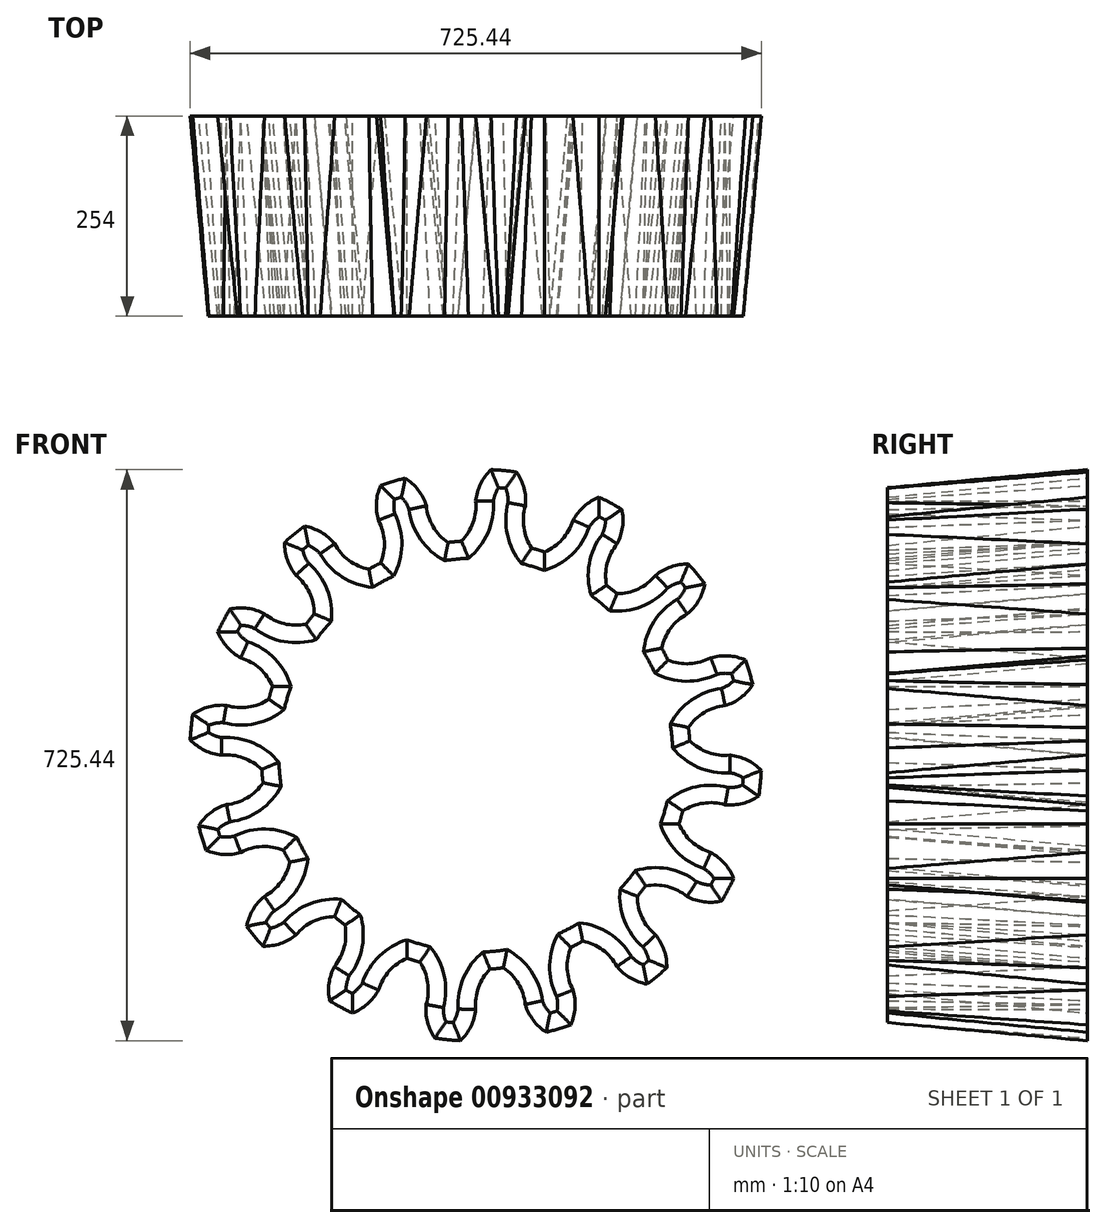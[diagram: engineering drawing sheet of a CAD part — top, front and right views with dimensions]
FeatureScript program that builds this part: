
annotation { "Feature Type Name" : "Feature", "Feature Type Description" : "" }
export const myFeature = defineFeature(function(context is Context, id is Id, definition is map)
    precondition{}
    {
        {
            var Q0;
            Q0=qCreatedBy(makeId("Front.planeOp"),FACE);
            var sketch = newSketch(context, id + "F0", { "sketchPlane" : qUnion([Q0])});
            skArc(sketch, "E0", {"start": v(19.52, 362.72) * mm, "mid": v(6.16, 344.56) * mm, "end": v(0, 322.88) * mm});
            skArc(sketch, "E1", {"start": v(63.13, 316.65) * mm, "mid": v(61.06, 288.95) * mm, "end": v(71.04, 263.02) * mm});
            skArc(sketch, "E2", {"start": v(51.78, 359.54) * mm, "mid": v(35.68, 361.49) * mm, "end": v(19.52, 362.72) * mm});
            skCircle(sketch, "E3", {"center": v(0, 0) * mm, "radius": 272.44 * mm});
            skArc(sketch, "E4.trimOffspring", {"start": v(-18.24, 271.83) * mm, "mid": v(-3.4, 295.31) * mm, "end": v(0, 322.88) * mm});
            skArc(sketch, "E5.trimOffspring", {"start": v(63.13, 316.65) * mm, "mid": v(61.32, 339.12) * mm, "end": v(51.78, 359.54) * mm});
            skArc(sketch, "E6.1.0", {"start": v(-89.75, 351.98) * mm, "mid": v(-105.37, 347.63) * mm, "end": v(-120.77, 342.58) * mm});
            skArc(sketch, "E6.1.1", {"start": v(-62.85, 316.7) * mm, "mid": v(-73.12, 336.77) * mm, "end": v(-89.75, 351.98) * mm});
            skArc(sketch, "E6.1.2", {"start": v(-62.85, 316.7) * mm, "mid": v(-54.16, 290.32) * mm, "end": v(-35.02, 270.18) * mm});
            skArc(sketch, "E6.1.4", {"start": v(-120.88, 244.16) * mm, "mid": v(-116.14, 271.53) * mm, "end": v(-123.56, 298.3) * mm});
            skArc(sketch, "E6.1.5", {"start": v(-120.77, 342.58) * mm, "mid": v(-126.16, 320.7) * mm, "end": v(-123.56, 298.3) * mm});
            skArc(sketch, "E6.2.0", {"start": v(-217.62, 290.84) * mm, "mid": v(-230.38, 280.84) * mm, "end": v(-242.68, 270.28) * mm});
            skArc(sketch, "E6.2.1", {"start": v(-179.27, 268.55) * mm, "mid": v(-196.43, 283.16) * mm, "end": v(-217.62, 290.84) * mm});
            skArc(sketch, "E6.2.2", {"start": v(-179.27, 268.55) * mm, "mid": v(-161.14, 247.5) * mm, "end": v(-135.75, 236.21) * mm});
            skArc(sketch, "E6.2.4", {"start": v(-205.11, 179.31) * mm, "mid": v(-211.21, 206.42) * mm, "end": v(-228.31, 228.31) * mm});
            skArc(sketch, "E6.2.5", {"start": v(-242.68, 270.28) * mm, "mid": v(-239.29, 248) * mm, "end": v(-228.31, 228.31) * mm});
            skArc(sketch, "E7.1.3.0", {"start": v(-312.35, 185.42) * mm, "mid": v(-320.32, 171.3) * mm, "end": v(-327.64, 156.84) * mm});
            skArc(sketch, "E7.4.3.0", {"start": v(-268.4, 179.5) * mm, "mid": v(-289.84, 186.43) * mm, "end": v(-312.35, 185.42) * mm});
            skArc(sketch, "E7.8.3.0", {"start": v(-268.4, 179.5) * mm, "mid": v(-243.58, 167) * mm, "end": v(-215.81, 166.28) * mm});
            skArc(sketch, "E7.12.3.0", {"start": v(271.83, 18.24) * mm, "mid": v(-271.12, 26.76) * mm, "end": v(263.02, -71.04) * mm});
            skArc(sketch, "E7.14.3.0", {"start": v(-258.12, 87.17) * mm, "mid": v(-274.13, 109.88) * mm, "end": v(-298.3, 123.56) * mm});
            skArc(sketch, "E7.18.3.0", {"start": v(-327.64, 156.84) * mm, "mid": v(-315.98, 137.55) * mm, "end": v(-298.3, 123.56) * mm});
            skArc(sketch, "E7.1.4.0", {"start": v(-359.54, 51.78) * mm, "mid": v(-361.49, 35.68) * mm, "end": v(-362.72, 19.52) * mm});
            skArc(sketch, "E7.4.4.0", {"start": v(-316.65, 63.13) * mm, "mid": v(-339.12, 61.32) * mm, "end": v(-359.54, 51.78) * mm});
            skArc(sketch, "E7.8.4.0", {"start": v(-316.65, 63.13) * mm, "mid": v(-288.95, 61.06) * mm, "end": v(-263.02, 71.04) * mm});
            skArc(sketch, "E7.14.4.0", {"start": v(-271.83, -18.24) * mm, "mid": v(-295.31, -3.4) * mm, "end": v(-322.88, 0) * mm});
            skArc(sketch, "E7.18.4.0", {"start": v(-362.72, 19.52) * mm, "mid": v(-344.56, 6.16) * mm, "end": v(-322.88, 0) * mm});
            skArc(sketch, "E7.1.5.0", {"start": v(-351.98, -89.75) * mm, "mid": v(-347.63, -105.37) * mm, "end": v(-342.58, -120.77) * mm});
            skArc(sketch, "E7.4.5.0", {"start": v(-316.7, -62.85) * mm, "mid": v(-336.77, -73.12) * mm, "end": v(-351.98, -89.75) * mm});
            skArc(sketch, "E7.8.5.0", {"start": v(-316.7, -62.85) * mm, "mid": v(-290.32, -54.16) * mm, "end": v(-270.18, -35.02) * mm});
            skArc(sketch, "E7.14.5.0", {"start": v(-244.16, -120.88) * mm, "mid": v(-271.53, -116.14) * mm, "end": v(-298.3, -123.56) * mm});
            skArc(sketch, "E7.18.5.0", {"start": v(-342.58, -120.77) * mm, "mid": v(-320.7, -126.16) * mm, "end": v(-298.3, -123.56) * mm});
            skArc(sketch, "E7.1.6.0", {"start": v(-290.84, -217.62) * mm, "mid": v(-280.84, -230.38) * mm, "end": v(-270.28, -242.68) * mm});
            skArc(sketch, "E7.4.6.0", {"start": v(-268.55, -179.27) * mm, "mid": v(-283.16, -196.43) * mm, "end": v(-290.84, -217.62) * mm});
            skArc(sketch, "E7.8.6.0", {"start": v(-268.55, -179.27) * mm, "mid": v(-247.5, -161.14) * mm, "end": v(-236.21, -135.75) * mm});
            skArc(sketch, "E7.14.6.0", {"start": v(-179.31, -205.11) * mm, "mid": v(-206.42, -211.21) * mm, "end": v(-228.31, -228.31) * mm});
            skArc(sketch, "E7.18.6.0", {"start": v(-270.28, -242.68) * mm, "mid": v(-248, -239.29) * mm, "end": v(-228.31, -228.31) * mm});
            skArc(sketch, "E7.1.7.0", {"start": v(-185.42, -312.35) * mm, "mid": v(-171.3, -320.32) * mm, "end": v(-156.84, -327.64) * mm});
            skArc(sketch, "E7.4.7.0", {"start": v(-179.5, -268.4) * mm, "mid": v(-186.43, -289.84) * mm, "end": v(-185.42, -312.35) * mm});
            skArc(sketch, "E7.8.7.0", {"start": v(-179.5, -268.4) * mm, "mid": v(-167, -243.58) * mm, "end": v(-166.28, -215.81) * mm});
            skArc(sketch, "E7.14.7.0", {"start": v(-87.17, -258.12) * mm, "mid": v(-109.88, -274.13) * mm, "end": v(-123.56, -298.3) * mm});
            skArc(sketch, "E7.18.7.0", {"start": v(-156.84, -327.64) * mm, "mid": v(-137.55, -315.98) * mm, "end": v(-123.56, -298.3) * mm});
            skArc(sketch, "E7.1.8.0", {"start": v(-51.78, -359.54) * mm, "mid": v(-35.68, -361.49) * mm, "end": v(-19.52, -362.72) * mm});
            skArc(sketch, "E7.4.8.0", {"start": v(-63.13, -316.65) * mm, "mid": v(-61.32, -339.12) * mm, "end": v(-51.78, -359.54) * mm});
            skArc(sketch, "E7.8.8.0", {"start": v(-63.13, -316.65) * mm, "mid": v(-61.06, -288.95) * mm, "end": v(-71.04, -263.02) * mm});
            skArc(sketch, "E7.12.8.0", {"start": v(271.83, 18.24) * mm, "mid": v(-260.7, 79.14) * mm, "end": v(215.81, -166.28) * mm});
            skArc(sketch, "E7.14.8.0", {"start": v(18.24, -271.83) * mm, "mid": v(3.4, -295.31) * mm, "end": v(0, -322.88) * mm});
            skArc(sketch, "E7.18.8.0", {"start": v(-19.52, -362.72) * mm, "mid": v(-6.16, -344.56) * mm, "end": v(0, -322.88) * mm});
            skArc(sketch, "E7.1.9.0", {"start": v(89.75, -351.98) * mm, "mid": v(105.37, -347.63) * mm, "end": v(120.77, -342.58) * mm});
            skArc(sketch, "E7.4.9.0", {"start": v(62.85, -316.7) * mm, "mid": v(73.12, -336.77) * mm, "end": v(89.75, -351.98) * mm});
            skArc(sketch, "E7.8.9.0", {"start": v(62.85, -316.7) * mm, "mid": v(54.16, -290.32) * mm, "end": v(35.02, -270.18) * mm});
            skArc(sketch, "E7.14.9.0", {"start": v(120.88, -244.16) * mm, "mid": v(116.14, -271.53) * mm, "end": v(123.56, -298.3) * mm});
            skArc(sketch, "E7.18.9.0", {"start": v(120.77, -342.58) * mm, "mid": v(126.16, -320.7) * mm, "end": v(123.56, -298.3) * mm});
            skArc(sketch, "E7.1.10.0", {"start": v(217.62, -290.84) * mm, "mid": v(230.38, -280.84) * mm, "end": v(242.68, -270.28) * mm});
            skArc(sketch, "E7.4.10.0", {"start": v(179.27, -268.55) * mm, "mid": v(196.43, -283.16) * mm, "end": v(217.62, -290.84) * mm});
            skArc(sketch, "E7.8.10.0", {"start": v(179.27, -268.55) * mm, "mid": v(161.14, -247.5) * mm, "end": v(135.75, -236.21) * mm});
            skArc(sketch, "E7.14.10.0", {"start": v(205.11, -179.31) * mm, "mid": v(211.21, -206.42) * mm, "end": v(228.31, -228.31) * mm});
            skArc(sketch, "E7.18.10.0", {"start": v(242.68, -270.28) * mm, "mid": v(239.29, -248) * mm, "end": v(228.31, -228.31) * mm});
            skArc(sketch, "E7.1.11.0", {"start": v(312.35, -185.42) * mm, "mid": v(320.32, -171.3) * mm, "end": v(327.64, -156.84) * mm});
            skArc(sketch, "E7.4.11.0", {"start": v(268.4, -179.5) * mm, "mid": v(289.84, -186.43) * mm, "end": v(312.35, -185.42) * mm});
            skArc(sketch, "E7.8.11.0", {"start": v(268.4, -179.5) * mm, "mid": v(243.58, -167) * mm, "end": v(215.81, -166.28) * mm});
            skArc(sketch, "E7.14.11.0", {"start": v(258.12, -87.17) * mm, "mid": v(274.13, -109.88) * mm, "end": v(298.3, -123.56) * mm});
            skArc(sketch, "E7.18.11.0", {"start": v(327.64, -156.84) * mm, "mid": v(315.98, -137.55) * mm, "end": v(298.3, -123.56) * mm});
            skArc(sketch, "E7.1.12.0", {"start": v(359.54, -51.78) * mm, "mid": v(361.49, -35.68) * mm, "end": v(362.72, -19.52) * mm});
            skArc(sketch, "E7.4.12.0", {"start": v(316.65, -63.13) * mm, "mid": v(339.12, -61.32) * mm, "end": v(359.54, -51.78) * mm});
            skArc(sketch, "E7.8.12.0", {"start": v(316.65, -63.13) * mm, "mid": v(288.95, -61.06) * mm, "end": v(263.02, -71.04) * mm});
            skArc(sketch, "E7.14.12.0", {"start": v(271.83, 18.24) * mm, "mid": v(295.31, 3.4) * mm, "end": v(322.88, 0) * mm});
            skArc(sketch, "E7.18.12.0", {"start": v(362.72, -19.52) * mm, "mid": v(344.56, -6.16) * mm, "end": v(322.88, 0) * mm});
            skArc(sketch, "E7.1.13.0", {"start": v(351.98, 89.75) * mm, "mid": v(347.63, 105.37) * mm, "end": v(342.58, 120.77) * mm});
            skArc(sketch, "E7.4.13.0", {"start": v(316.7, 62.85) * mm, "mid": v(336.77, 73.12) * mm, "end": v(351.98, 89.75) * mm});
            skArc(sketch, "E7.8.13.0", {"start": v(316.7, 62.85) * mm, "mid": v(290.32, 54.16) * mm, "end": v(270.18, 35.02) * mm});
            skArc(sketch, "E7.14.13.0", {"start": v(244.16, 120.88) * mm, "mid": v(271.53, 116.14) * mm, "end": v(298.3, 123.56) * mm});
            skArc(sketch, "E7.18.13.0", {"start": v(342.58, 120.77) * mm, "mid": v(320.7, 126.16) * mm, "end": v(298.3, 123.56) * mm});
            skArc(sketch, "E7.1.14.0", {"start": v(290.84, 217.62) * mm, "mid": v(280.84, 230.38) * mm, "end": v(270.28, 242.68) * mm});
            skArc(sketch, "E7.4.14.0", {"start": v(268.55, 179.27) * mm, "mid": v(283.16, 196.43) * mm, "end": v(290.84, 217.62) * mm});
            skArc(sketch, "E7.8.14.0", {"start": v(268.55, 179.27) * mm, "mid": v(247.5, 161.14) * mm, "end": v(236.21, 135.75) * mm});
            skArc(sketch, "E7.14.14.0", {"start": v(179.31, 205.11) * mm, "mid": v(206.42, 211.21) * mm, "end": v(228.31, 228.31) * mm});
            skArc(sketch, "E7.18.14.0", {"start": v(270.28, 242.68) * mm, "mid": v(248, 239.29) * mm, "end": v(228.31, 228.31) * mm});
            skArc(sketch, "E7.1.15.0", {"start": v(185.42, 312.35) * mm, "mid": v(171.3, 320.32) * mm, "end": v(156.84, 327.64) * mm});
            skArc(sketch, "E7.4.15.0", {"start": v(179.5, 268.4) * mm, "mid": v(186.43, 289.84) * mm, "end": v(185.42, 312.35) * mm});
            skArc(sketch, "E7.8.15.0", {"start": v(179.5, 268.4) * mm, "mid": v(167, 243.58) * mm, "end": v(166.28, 215.81) * mm});
            skArc(sketch, "E7.14.15.0", {"start": v(87.17, 258.12) * mm, "mid": v(109.88, 274.13) * mm, "end": v(123.56, 298.3) * mm});
            skArc(sketch, "E7.18.15.0", {"start": v(156.84, 327.64) * mm, "mid": v(137.55, 315.98) * mm, "end": v(123.56, 298.3) * mm});
            skArc(sketch, "E8.trimOffspring", {"start": v(258.12, -87.17) * mm, "mid": v(260.7, -79.14) * mm, "end": v(263.02, -71.04) * mm});
            skSolve(sketch);
        }
        {
            var Q0;
            Q0=makeQuery(id+"F0.imprint","IMPRINT",FACE,{"disambiguationData":[TD([[makeQuery(id+"F0.imprint","IMPRINT",EDGE,{"derivedFrom":sQuery(id+"F0.wireOp",EDGE,"E7.1.15.0")}),1.0]])]});
            var Q1;
            Q1=makeQuery(id+"F0.imprint","IMPRINT",FACE,{"disambiguationData":[TD([[makeQuery(id+"F0.imprint","IMPRINT",EDGE,{"derivedFrom":sQuery(id+"F0.wireOp",EDGE,"E7.1.13.0")}),1.0]])]});
            var Q2;
            Q2=makeQuery(id+"F0.imprint","IMPRINT",FACE,{"disambiguationData":[TD([[makeQuery(id+"F0.imprint","IMPRINT",EDGE,{"derivedFrom":sQuery(id+"F0.wireOp",EDGE,"E7.1.14.0")}),1.0]])]});
            var Q3;
            Q3=makeQuery(id+"F0.imprint","IMPRINT",FACE,{"disambiguationData":[TD([[makeQuery(id+"F0.imprint","IMPRINT",EDGE,{"derivedFrom":sQuery(id+"F0.wireOp",EDGE,"E0")}),1.0]])]});
            var Q4;
            Q4=makeQuery(id+"F0.imprint","IMPRINT",FACE,{"disambiguationData":[TD([[makeQuery(id+"F0.imprint","IMPRINT",EDGE,{"derivedFrom":sQuery(id+"F0.wireOp",EDGE,"E6.1.0")}),1.0]])]});
            var Q5;
            Q5=makeQuery(id+"F0.imprint","IMPRINT",FACE,{"disambiguationData":[TD([[makeQuery(id+"F0.imprint","IMPRINT",EDGE,{"derivedFrom":sQuery(id+"F0.wireOp",EDGE,"E6.2.0")}),1.0]])]});
            var Q6;
            Q6=makeQuery(id+"F0.imprint","IMPRINT",FACE,{"disambiguationData":[TD([[makeQuery(id+"F0.imprint","IMPRINT",EDGE,{"derivedFrom":sQuery(id+"F0.wireOp",EDGE,"E7.1.3.0")}),1.0]])]});
            var Q7;
            Q7=makeQuery(id+"F0.imprint","IMPRINT",FACE,{"disambiguationData":[TD([[makeQuery(id+"F0.imprint","IMPRINT",EDGE,{"derivedFrom":sQuery(id+"F0.wireOp",EDGE,"E7.1.4.0")}),1.0]])]});
            var Q8;
            Q8=makeQuery(id+"F0.imprint","IMPRINT",FACE,{"disambiguationData":[TD([[makeQuery(id+"F0.imprint","IMPRINT",EDGE,{"derivedFrom":sQuery(id+"F0.wireOp",EDGE,"E7.1.5.0")}),1.0]])]});
            var Q9;
            Q9=makeQuery(id+"F0.imprint","IMPRINT",FACE,{"disambiguationData":[TD([[makeQuery(id+"F0.imprint","IMPRINT",EDGE,{"derivedFrom":sQuery(id+"F0.wireOp",EDGE,"E7.1.6.0")}),1.0]])]});
            var Q10;
            Q10=makeQuery(id+"F0.imprint","IMPRINT",FACE,{"disambiguationData":[TD([[makeQuery(id+"F0.imprint","IMPRINT",EDGE,{"derivedFrom":sQuery(id+"F0.wireOp",EDGE,"E7.1.7.0")}),1.0]])]});
            var Q11;
            Q11=makeQuery(id+"F0.imprint","IMPRINT",FACE,{"disambiguationData":[TD([[makeQuery(id+"F0.imprint","IMPRINT",EDGE,{"derivedFrom":sQuery(id+"F0.wireOp",EDGE,"E7.1.8.0")}),1.0]])]});
            var Q12;
            Q12=makeQuery(id+"F0.imprint","IMPRINT",FACE,{"disambiguationData":[TD([[makeQuery(id+"F0.imprint","IMPRINT",EDGE,{"derivedFrom":sQuery(id+"F0.wireOp",EDGE,"E7.1.9.0")}),1.0]])]});
            var Q13;
            Q13=makeQuery(id+"F0.imprint","IMPRINT",FACE,{"disambiguationData":[TD([[makeQuery(id+"F0.imprint","IMPRINT",EDGE,{"derivedFrom":sQuery(id+"F0.wireOp",EDGE,"E7.1.10.0")}),1.0]])]});
            var Q14;
            Q14=makeQuery(id+"F0.imprint","IMPRINT",FACE,{"disambiguationData":[TD([[makeQuery(id+"F0.imprint","IMPRINT",EDGE,{"derivedFrom":sQuery(id+"F0.wireOp",EDGE,"E7.1.11.0")}),1.0]])]});
            var Q15;
            Q15=makeQuery(id+"F0.imprint","IMPRINT",FACE,{"disambiguationData":[TD([[makeQuery(id+"F0.imprint","IMPRINT",EDGE,{"derivedFrom":sQuery(id+"F0.wireOp",EDGE,"E7.1.12.0")}),1.0]])]});
            var Q16;
            {var subQ0=sQuery(id+"F0.wireOp",EDGE,"E3");var subQ18=makeQuery(id+"F0.imprint","INTERSECT",VERTEX,{"derivedFrom":[sQuery(id+"F0.wireOp",EDGE,"E7.14.11.0"),subQ0]});Q16=makeQuery(id+"F0.imprint","IMPRINT",FACE,{"disambiguationData":[TD([[makeQuery(id+"F0.imprint","IMPRINT",EDGE,{"disambiguationData":[TD([[subQ18,-1.0]])],"derivedFrom":subQ0}),1.0]])]});}
            extrude(context, id + "F1", {"entities" : qUnion([Q0, Q1, Q2, Q3, Q4, Q5, Q6, Q7, Q8, Q9, Q10, Q11, Q12, Q13, Q14, Q15, Q16]), "depth" : 254 * mm, "offsetDistance" : 25.4 * mm, "hasDraft" : true, "draftAngle" : 5 * degree, "draftPullDirection" : true});
        }
    });
